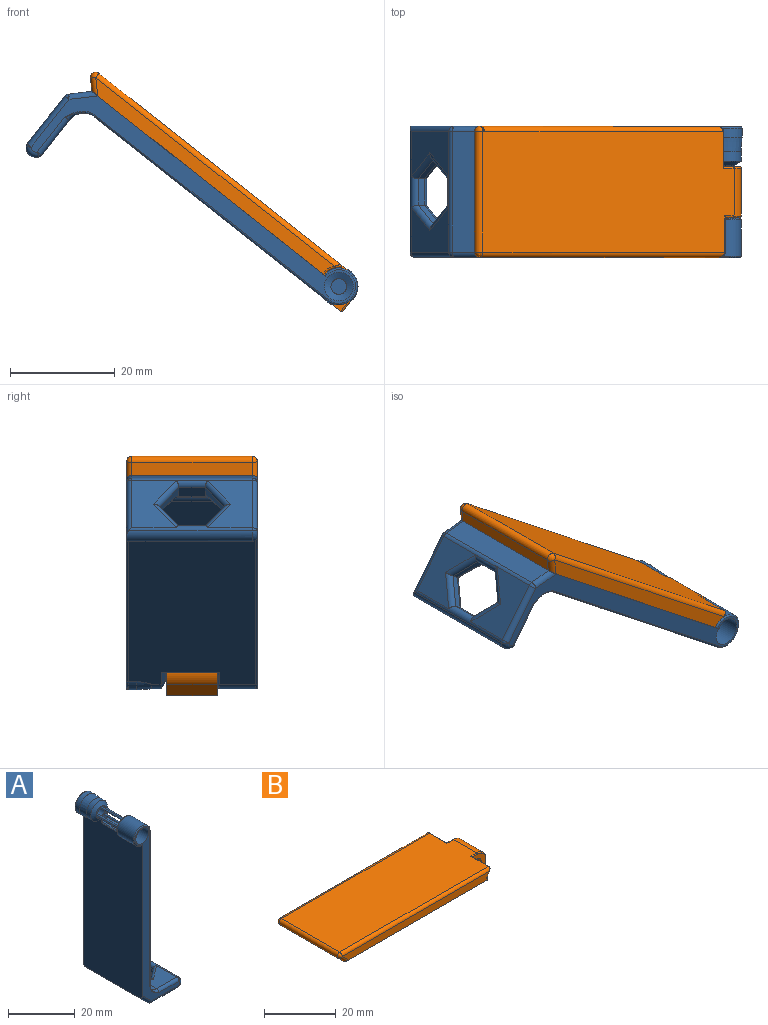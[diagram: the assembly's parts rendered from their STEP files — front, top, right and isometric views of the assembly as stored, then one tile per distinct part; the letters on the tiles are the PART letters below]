
ASSEMBLY  parts=2 mates=1
PART A: 84 faces, bbox 21.4x38.6x68 mm
  f0: cylinder r=1.5mm len=3.5mm, axis (0,-1,0), area 33mm2, adj f11,f12,f13,f16,f83
  f1: plane 57.08x24.93mm, normal (1,0,0), area 1330.4mm2, adj f3,f7,f14,f18,f49,f50,f70,f71
  f2: plane 58.32x25.42mm, normal (-1,0,0), area 1407.5mm2, adj f3,f8,f9,f14,f15,f16,f17,f33
  f3: cylinder r=3.5mm len=7mm, axis (0,1,0), area 29.7mm2, adj f1,f2,f17,f70
  f4: plane 8.52x8.51mm, normal (0,0,1), area 50.4mm2, adj f7,f35,f38,f60,f62
  f5: plane 23x11.6mm, normal (0,0,-1), area 146.9mm2, adj f40,f44,f46,f48,f64,f65,f66,f67
  f6: plane 8.52x8.51mm, normal (0,0,1), area 50.4mm2, adj f7,f37,f38,f57,f58
  f7: cylinder r=3.5mm len=23mm, axis (0,-1,0), area 105.3mm2, adj f1,f4,f6,f49,f50,f59,f61,f63
  f8: plane 66.28x20.68mm, normal (0,1,0), area 218.2mm2, adj f2,f24,f25,f26,f27,f28,f29,f34
  f9: plane 65.7x19.1mm, normal (0,-1,0), area 216.3mm2, adj f2,f31,f36,f37,f44,f45,f72,f73
  f10: cylinder r=1.5mm len=3.1mm, axis (0,-1,0), area 29.2mm2, adj f15,f32
  f11: plane 2.1x2.1mm, normal (0,-1,0), area 1.4mm2, adj f0,f17,f19,f23
  f12: plane 1.94x1.53mm, normal (0,-1,0), area 1mm2, adj f0,f17,f22,f23
  f13: plane 1.94x1.53mm, normal (0,-1,0), area 1mm2, adj f0,f17,f19,f20
  f14: cylinder r=3.5mm len=7mm, axis (0,1,0), area 113.8mm2, adj f1,f2,f72,f79
  f15: plane 7.15x6.4mm, normal (0,1,0), area 27.3mm2, adj f2,f10,f19,f20,f21,f22,f23,f69
  f16: plane 4.75x2.9mm, normal (0,-1,0), area 6.2mm2, adj f0,f2,f17,f18,f20,f21,f22,f69
  f17: cone r=2.1mm half-angle=57.3deg, axis (0,1,0), area 22mm2, adj f2,f3,f11,f12,f13,f16,f18
  f18: plane 4.03x1.48mm, normal (0.54,-0.84,0), area 6.1mm2, adj f1,f16,f17,f69,f80
  f19: cylinder r=0.3mm len=10mm, axis (0,1,0), area 18.8mm2, adj f11,f13,f15
  f20: cylinder r=0.3mm len=10mm, axis (0,1,0), area 18.8mm2, adj f13,f15,f16
  f21: cylinder r=0.3mm len=10mm, axis (0,1,0), area 18.8mm2, adj f15,f16
  f22: cylinder r=0.3mm len=10mm, axis (0,1,0), area 18.8mm2, adj f12,f15,f16
  f23: cylinder r=0.3mm len=10mm, axis (0,1,0), area 18.8mm2, adj f11,f12,f15
  f24: plane 3.8x3.18mm, normal (0,0,-1), area 12.1mm2, adj f8,f25,f29,f30
  f25: plane 3.8x2.75mm, normal (-0.87,0,-0.5), area 12.1mm2, adj f8,f24,f26,f30
  f26: plane 3.8x2.75mm, normal (-0.87,0,0.5), area 12.1mm2, adj f8,f25,f27,f30
  f27: plane 3.8x3.18mm, normal (0,0,1), area 12.1mm2, adj f8,f26,f28,f30
  f28: plane 3.8x2.75mm, normal (0.87,0,0.5), area 12.1mm2, adj f8,f27,f29,f30
  f29: plane 3.8x2.75mm, normal (0.87,0,-0.5), area 12.1mm2, adj f8,f24,f28,f30
  f30: plane 6.35x5.5mm, normal (0,1,0), area 26.2mm2, adj f24,f25,f26,f27,f28,f29
  f31: cylinder r=2.75mm len=5.5mm, axis (0,-1,0), area 65.7mm2, adj f9,f32
  f32: cone r=1.5mm half-angle=64.4deg, axis (0,-1,0), area 18.5mm2, adj f10,f31
  f33: plane 23x3.21mm, normal (-0.71,0,-0.71), area 104.3mm2, adj f2,f36,f39,f40
  f34: cylinder r=1.93mm len=24mm, axis (0,-1,0), area 86.8mm2, adj f8,f35,f38,f45,f46,f48
  f35: cylinder r=1mm len=9.75mm, axis (-1,0,0), area 14.4mm2, adj f4,f8,f34,f38,f49
  f36: cylinder r=1mm len=4.62mm, axis (0.71,0,-0.71), area 7.9mm2, adj f2,f9,f33,f41
  f37: cylinder r=1mm len=8.52mm, axis (1,0,0), area 13.4mm2, adj f6,f9,f42,f50
  f38: cylinder r=1mm len=23.59mm, axis (0,-1,0), area 23.2mm2, adj f4,f6,f34,f35,f42,f52,f57,f60
  f39: cylinder r=1mm len=4.62mm, axis (0.71,0,-0.71), area 7.9mm2, adj f2,f8,f33,f43
  f40: cylinder r=1mm len=23mm, axis (0,1,0), area 18.1mm2, adj f5,f33,f41,f43
  f41: sphere r=1mm, area 1mm2, adj f36,f40,f44
  f42: sphere r=1mm, area 0.6mm2, adj f37,f38,f45
  f43: sphere r=1mm, area 1mm2, adj f39,f40,f46
  f44: cylinder r=1mm len=11.6mm, axis (-1,0,0), area 18.2mm2, adj f5,f9,f41,f47
  f45: torus R=0.93mm, axis (0,-1,0), area 4.6mm2, adj f9,f34,f42,f47
  f46: cylinder r=1mm len=12.83mm, axis (1,0,0), area 19.3mm2, adj f5,f8,f34,f43,f48
  f47: sphere r=1mm, area 0.6mm2, adj f44,f45,f48
  f48: cylinder r=1mm len=23.59mm, axis (0,-1,0), area 23.2mm2, adj f5,f34,f46,f47,f52,f65,f68
  f49: torus R=4.5mm, axis (1,0,0), area 4.9mm2, adj f1,f7,f35,f77
  f50: torus R=4.5mm, axis (1,0,0), area 4.9mm2, adj f1,f7,f37,f74
  f51: plane 5.12x2.66mm, normal (1,0,0), area 13.2mm2, adj f53,f56,f59,f61,f63,f66
  f52: plane 5x1.5mm, normal (-1,0,0), area 7.5mm2, adj f38,f48,f54,f55
  f53: plane 4.76x3.66mm, normal (0.61,0.79,0), area 9.9mm2, adj f51,f54,f58,f59,f64
  f54: plane 4.76x3.66mm, normal (-0.61,0.79,0), area 9mm2, adj f52,f53,f57,f65
  f55: plane 4.76x3.66mm, normal (-0.61,-0.79,0), area 9mm2, adj f52,f56,f60,f68
  f56: plane 4.76x3.66mm, normal (0.61,-0.79,0), area 9.9mm2, adj f51,f55,f62,f63,f67
  f57: cylinder r=1mm len=6.37mm, axis (0.79,0.61,0), area 10.4mm2, adj f6,f38,f54,f58
  f58: cylinder r=1mm len=3.37mm, axis (-0.79,0.61,0), area 4.9mm2, adj f6,f53,f57,f59
  f59: bspline ~4.1x3.95mm, area 4.6mm2, adj f7,f51,f53,f58,f61
  f60: cylinder r=1mm len=6.37mm, axis (0.79,-0.61,0), area 10.4mm2, adj f4,f38,f55,f62
  f61: cylinder r=1mm len=5.99mm, axis (0,-1,0), area 4.7mm2, adj f7,f51,f59,f63
  f62: cylinder r=1mm len=3.37mm, axis (-0.79,-0.61,0), area 4.9mm2, adj f4,f56,f60,f63
  f63: bspline ~4.1x3.95mm, area 4.6mm2, adj f7,f51,f56,f61,f62
  f64: cylinder r=1mm len=6.37mm, axis (0.79,-0.61,0), area 10.4mm2, adj f5,f53,f65,f66
  f65: cylinder r=1mm len=6.37mm, axis (-0.79,-0.61,0), area 10.4mm2, adj f5,f48,f54,f64
  f66: cylinder r=1mm len=5.99mm, axis (0,-1,0), area 8.6mm2, adj f5,f51,f64,f67
  f67: cylinder r=1mm len=6.37mm, axis (0.79,0.61,0), area 10.4mm2, adj f5,f56,f66,f68
  f68: cylinder r=1mm len=6.37mm, axis (-0.79,0.61,0), area 10.4mm2, adj f5,f48,f55,f67
  f69: plane 10.71x2.9mm, normal (0,0,1), area 29.4mm2, adj f15,f16,f18,f80,f82
  f70: cone r=3.5mm half-angle=3.5deg, axis (0,1,0), area 48.8mm2, adj f1,f2,f3,f78
  f71: cylinder r=3.67mm len=7.34mm, axis (0,-1,0), area 31.2mm2, adj f1,f2,f75,f78
  f72: torus R=3.2mm, axis (0,-1,0), area 7.5mm2, adj f2,f9,f14,f73
  f73: cylinder r=0.3mm len=56.55mm, axis (0,0,-1), area 26.7mm2, adj f1,f9,f72,f74
  f74: bspline ~5.2x3.8mm, area 1.2mm2, adj f9,f50,f73
  f75: torus R=3.37mm, axis (0,-1,0), area 8.4mm2, adj f2,f8,f71,f76
  f76: cylinder r=0.3mm len=55.49mm, axis (0,0,1), area 26.1mm2, adj f1,f8,f75,f77
  f77: bspline ~5.2x3.8mm, area 1.2mm2, adj f8,f49,f76
  f78: torus R=3.37mm, axis (0,1,0), area 0.3mm2, adj f1,f2,f70,f71
  f79: torus R=3.2mm, axis (0,-1,0), area 7.5mm2, adj f2,f14,f15,f81
  f80: cylinder r=0.3mm len=11.2mm, axis (0,1,0), area 5.2mm2, adj f1,f18,f69,f81
  f81: cylinder r=0.3mm len=3.95mm, axis (0,0,1), area 1.8mm2, adj f1,f15,f79,f80
  f82: cylinder r=0.3mm len=10mm, axis (0,-1,0), area 4.7mm2, adj f2,f15,f16,f69
  f83: plane 3x3mm, normal (0,-1,0), area 7.1mm2, adj f0
PART B: 35 faces, bbox 66.3x25.5x7.7 mm
  f0: cylinder r=3.5mm len=9.7mm, axis (0,1,0), area 53.3mm2, adj f2,f4,f8,f12
  f1: cylinder r=3.5mm len=9.1mm, axis (0,1,0), area 50.4mm2, adj f7,f13,f26,f30
  f2: plane 6.85x6.7mm, normal (0,-1,0), area 31.7mm2, adj f0,f3,f5,f8,f12,f29,f30,f31
  f3: cylinder r=1.5mm len=9.7mm, axis (0,-1,0), area 91.4mm2, adj f2,f4
  f4: plane 7.05x6.7mm, normal (0,1,0), area 32.5mm2, adj f0,f3,f6,f8,f12,f24,f25,f26
  f5: cylinder r=3.65mm len=7.35mm, axis (0,1,0), area 25mm2, adj f2,f8,f32,f33,f34
  f6: cylinder r=3.85mm len=7.35mm, axis (0,1,0), area 24.6mm2, adj f4,f8,f22,f23,f24
  f7: plane 61.09x23mm, normal (0,0,1), area 1370.5mm2, adj f1,f16,f18,f19,f24,f25,f31,f32
  f8: plane 56.92x25.42mm, normal (0,0,-1), area 1408mm2, adj f0,f2,f4,f5,f6,f9,f10,f11
  f9: plane 58.03x2.5mm, normal (0,-1,0), area 140.4mm2, adj f8,f19,f21,f34
  f10: plane 57.77x2.5mm, normal (0,1,0), area 139.9mm2, adj f8,f15,f16,f22
  f11: plane 23x1.79mm, normal (-0.71,0,-0.71), area 58.3mm2, adj f8,f15,f18,f21
  f12: plane 9.7x3.2mm, normal (0,0,-1), area 31mm2, adj f0,f2,f4,f28
  f13: plane 9.1x0mm, normal (0,0,1), area 0mm2, adj f1,f14
  f14: plane 9.1x3.16mm, normal (1,0,0), area 28.8mm2, adj f13,f27,f28,f29
  f15: cylinder r=1mm len=3.21mm, axis (0.71,0,-0.71), area 4.8mm2, adj f8,f10,f11,f17
  f16: cylinder r=1mm len=58.44mm, axis (-1,0,0), area 91.3mm2, adj f7,f10,f17,f23
  f17: sphere r=1mm, area 2.7mm2, adj f15,f16,f18
  f18: cylinder r=1mm len=23mm, axis (0,-1,0), area 54.2mm2, adj f7,f11,f17,f20
  f19: cylinder r=1mm len=58.77mm, axis (1,0,0), area 91.7mm2, adj f7,f9,f20,f33
  f20: sphere r=1mm, area 1.6mm2, adj f18,f19,f21
  f21: cylinder r=1mm len=3.21mm, axis (0.71,0,-0.71), area 4.8mm2, adj f8,f9,f11,f20
  f22: torus R=4.15mm, axis (0,-1,0), area 1.2mm2, adj f6,f8,f10,f23
  f23: bspline ~1.64x1.41mm, area 1mm2, adj f6,f16,f22,f24
  f24: cylinder r=0.3mm len=6.95mm, axis (0,1,0), area 5mm2, adj f4,f6,f7,f23,f25
  f25: cylinder r=0.3mm len=2.64mm, axis (1,0,0), area 1.2mm2, adj f4,f7,f24,f26
  f26: torus R=3.2mm, axis (0,-1,0), area 2.5mm2, adj f1,f4,f25,f27
  f27: cylinder r=0.3mm len=3.46mm, axis (0,0,1), area 1.6mm2, adj f4,f14,f26,f28
  f28: cylinder r=0.3mm len=9.7mm, axis (0,1,0), area 4.4mm2, adj f12,f14,f27,f29
  f29: cylinder r=0.3mm len=3.47mm, axis (0,0,1), area 1.6mm2, adj f2,f14,f28,f30
  f30: torus R=3.2mm, axis (0,-1,0), area 2.5mm2, adj f1,f2,f29,f31
  f31: cylinder r=0.3mm len=2.32mm, axis (1,0,0), area 1mm2, adj f2,f7,f30,f32
  f32: cylinder r=0.3mm len=6.95mm, axis (0,1,0), area 5.1mm2, adj f2,f5,f7,f31,f33
  f33: bspline ~1.81x1.41mm, area 1mm2, adj f5,f19,f32,f34
  f34: torus R=3.95mm, axis (0,-1,0), area 1.2mm2, adj f5,f8,f9,f33
PLACE A rot(axis=(0,1,0),128.3deg) t=(-97.54,-1.89,36.56)mm
PLACE B rot(axis=(0,1,0),38.3deg) t=(-75.49,-1.89,-30.34)mm
MATE revolute B.f0 <-> A.f0  axis (0,-1,0) through (-53.07,-6.74,14.13)mm
